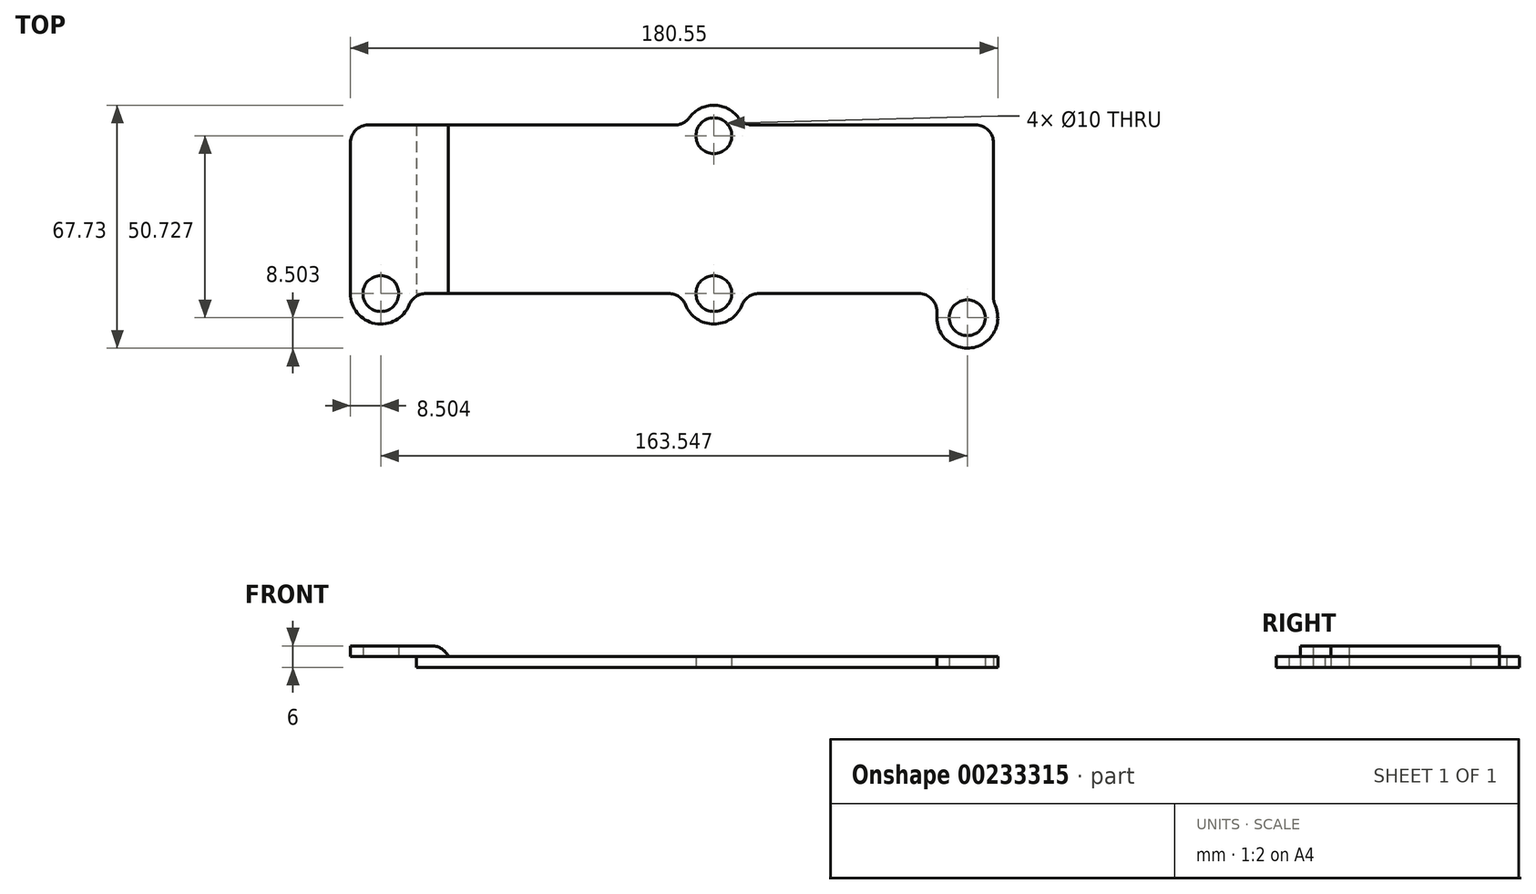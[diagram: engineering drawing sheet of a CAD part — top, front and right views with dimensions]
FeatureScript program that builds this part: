
annotation { "Feature Type Name" : "Feature", "Feature Type Description" : "" }
export const myFeature = defineFeature(function(context is Context, id is Id, definition is map)
    precondition{}
    {
        {
            var Q0;
            Q0=qCreatedBy(makeId("Top.planeOp"),FACE);
            var sketch = newSketch(context, id + "F0", { "sketchPlane" : qUnion([Q0])});
            skCircle(sketch, "E0", {"center": v(0, 0) * mm, "radius": 5 * mm});
            skCircle(sketch, "E1", {"center": v(-93, 0) * mm, "radius": 5 * mm});
            skCircle(sketch, "E2", {"center": v(0, 44) * mm, "radius": 5 * mm});
            skCircle(sketch, "E3", {"center": v(70.68, -6.73) * mm, "radius": 5 * mm});
            skLineSegment(sketch, "E4", {"start": v(-7.95, 47) * mm, "end": v(-83, 47) * mm});
            skLineSegment(sketch, "E5", {"start": v(0, 44) * mm, "end": v(-141.6, 44) * mm, "construction": true});
            skLineSegment(sketch, "E6", {"start": v(0, 44) * mm, "end": v(0, 51.47) * mm, "construction": true});
            skLineSegment(sketch, "E7", {"start": v(-83, 47) * mm, "end": v(-83, 0) * mm});
            skLineSegment(sketch, "E8", {"start": v(-83, 0) * mm, "end": v(-8.5, 0) * mm});
            skLineSegment(sketch, "E9", {"start": v(7.95, 47) * mm, "end": v(78, 47) * mm});
            skLineSegment(sketch, "E10", {"start": v(8.5, 0) * mm, "end": v(62.18, 0) * mm});
            skLineSegment(sketch, "E11", {"start": v(78, 47) * mm, "end": v(78, -2.4) * mm});
            skArc(sketch, "E12", {"start": v(7.95, 47) * mm, "mid": v(0, 52.5) * mm, "end": v(-7.95, 47) * mm});
            skArc(sketch, "E13", {"start": v(-8.5, 0) * mm, "mid": v(0, -8.5) * mm, "end": v(8.5, 0) * mm});
            skArc(sketch, "E14", {"start": v(62.18, -6.67) * mm, "mid": v(72.9, -14.93) * mm, "end": v(78, -2.4) * mm});
            skCircle(sketch, "E15", {"center": v(-93, 0) * mm, "radius": 8.5 * mm});
            skPoint(sketch, "E16.orphan", {"position": v(78, 0) * mm});
            skLineSegment(sketch, "E17", {"start": v(62.18, -6.78) * mm, "end": v(62.18, 0) * mm});
            skSolve(sketch);
        }
        {
            var Q0;
            Q0=makeQuery(id+"F0.imprint","IMPRINT",FACE,{"disambiguationData":[TD([[makeQuery(id+"F0.imprint","IMPRINT",EDGE,{"derivedFrom":sQuery(id+"F0.wireOp",EDGE,"E3")}),-1.0]])]});
            extrude(context, id + "F1", {"entities" : qUnion([Q0]), "depth" : 3 * mm});
        }
        {
            var Q0;
            Q0=makeQuery(id+"F1.opExtrude","CAP_FACE",FACE,{"disambiguationData":[OSD([sQuery(id+"F0.wireOp",EDGE,"E0"),sQuery(id+"F0.wireOp",EDGE,"E2"),sQuery(id+"F0.wireOp",EDGE,"E3"),sQuery(id+"F0.wireOp",EDGE,"E4"),sQuery(id+"F0.wireOp",EDGE,"E7"),sQuery(id+"F0.wireOp",EDGE,"E8"),sQuery(id+"F0.wireOp",EDGE,"E9"),sQuery(id+"F0.wireOp",EDGE,"E10"),sQuery(id+"F0.wireOp",EDGE,"E11"),sQuery(id+"F0.wireOp",EDGE,"E12"),sQuery(id+"F0.wireOp",EDGE,"E13"),sQuery(id+"F0.wireOp",EDGE,"E14"),sQuery(id+"F0.wireOp",EDGE,"E17")])],"isStart":false});
            var sketch = newSketch(context, id + "F2", { "sketchPlane" : qUnion([Q0])});
            skLineSegment(sketch, "E18.bottom", {"start": v(-74, 0) * mm, "end": v(-84.37, 0) * mm});
            skLineSegment(sketch, "E18.top", {"start": v(-74, 47) * mm, "end": v(-101.37, 47) * mm});
            skLineSegment(sketch, "E18.left", {"start": v(-74, 0) * mm, "end": v(-74, 47) * mm});
            skLineSegment(sketch, "E18.right", {"start": v(-101.37, 0) * mm, "end": v(-101.37, 47) * mm});
            skLineSegment(sketch, "E19", {"start": v(-101.37, 0) * mm, "end": v(-101.37, 0) * mm});
            skLineSegment(sketch, "E20", {"start": v(-101.37, 0) * mm, "end": v(-101.37, 46.86) * mm, "construction": true});
            skArc(sketch, "E21", {"start": v(-101.37, 0) * mm, "mid": v(-92.87, -8.5) * mm, "end": v(-84.37, 0) * mm});
            skCircle(sketch, "E22", {"center": v(-92.87, 0) * mm, "radius": 5 * mm});
            skSolve(sketch);
        }
        {
            var Q0;
            {var subQ2=sQuery(id+"F2.wireOp",EDGE,"E18.left");Q0=makeQuery(id+"F2.imprint","IMPRINT",FACE,{"disambiguationData":[TD([[makeQuery(id+"F2.imprint","IMPRINT",EDGE,{"derivedFrom":subQ2}),1.0]])]});}
            var Q1;
            {var subQ1=sQuery(id+"F2.wireOp",EDGE,"E18.right");Q1=makeQuery(id+"F2.imprint","IMPRINT",FACE,{"disambiguationData":[TD([[makeQuery(id+"F2.imprint","IMPRINT",EDGE,{"derivedFrom":subQ1}),-1.0]])]});}
            extrude(context, id + "F3", {"entities" : qUnion([Q0, Q1]), "depth" : 3 * mm});
        }
        {
            var Q0;
            Q0=makeQuery(id+"F3.opExtrude","CAP_EDGE",EDGE,{"disambiguationData":[OSD([sQuery(id+"F2.wireOp",EDGE,"E18.left")])],"isStart":false});
            var Q1;
            Q1=makeQuery(id+"F1.opExtrude","SWEPT_EDGE",EDGE,{"disambiguationData":[OSD([sQuery(id+"F0.wireOp",EDGE,"E10"),sQuery(id+"F0.wireOp",EDGE,"E13")])]});
            var Q2;
            Q2=makeQuery(id+"F1.opExtrude","SWEPT_EDGE",EDGE,{"disambiguationData":[OSD([sQuery(id+"F0.wireOp",EDGE,"E8"),sQuery(id+"F0.wireOp",EDGE,"E13")])]});
            var Q3;
            Q3=makeQuery(id+"F1.opExtrude","SWEPT_EDGE",EDGE,{"disambiguationData":[OSD([sQuery(id+"F0.wireOp",EDGE,"E10"),sQuery(id+"F0.wireOp",EDGE,"E17")])]});
            var Q4;
            Q4=makeQuery(id+"F1.opExtrude","SWEPT_EDGE",EDGE,{"disambiguationData":[OSD([sQuery(id+"F0.wireOp",EDGE,"E11"),sQuery(id+"F0.wireOp",EDGE,"E14")])]});
            var Q5;
            Q5=makeQuery(id+"F1.opExtrude","SWEPT_EDGE",EDGE,{"disambiguationData":[OSD([sQuery(id+"F0.wireOp",EDGE,"E9"),sQuery(id+"F0.wireOp",EDGE,"E11")])]});
            var Q6;
            Q6=makeQuery(id+"F1.opExtrude","SWEPT_EDGE",EDGE,{"disambiguationData":[OSD([sQuery(id+"F0.wireOp",EDGE,"E9"),sQuery(id+"F0.wireOp",EDGE,"E12")])]});
            var Q7;
            Q7=makeQuery(id+"F1.opExtrude","SWEPT_EDGE",EDGE,{"disambiguationData":[OSD([sQuery(id+"F0.wireOp",EDGE,"E4"),sQuery(id+"F0.wireOp",EDGE,"E12")])]});
            var Q8;
            Q8=makeQuery(id+"F3.opExtrude","SWEPT_EDGE",EDGE,{"disambiguationData":[OSD([sQuery(id+"F2.wireOp",EDGE,"E18.top"),sQuery(id+"F2.wireOp",EDGE,"E18.right")])]});
            var Q9;
            Q9=makeQuery(id+"F3.opExtrude","SWEPT_EDGE",EDGE,{"disambiguationData":[OSD([sQuery(id+"F2.wireOp",EDGE,"E18.bottom"),sQuery(id+"F2.wireOp",EDGE,"E21")])]});
            fillet(context, id + "F4", {"entities" : qUnion([Q0, Q1, Q2, Q3, Q4, Q5, Q6, Q7, Q8, Q9]), "radius" : 5 * mm, "tangentPropagation" : true, "allowEdgeOverflow" : false});
        }
    });
